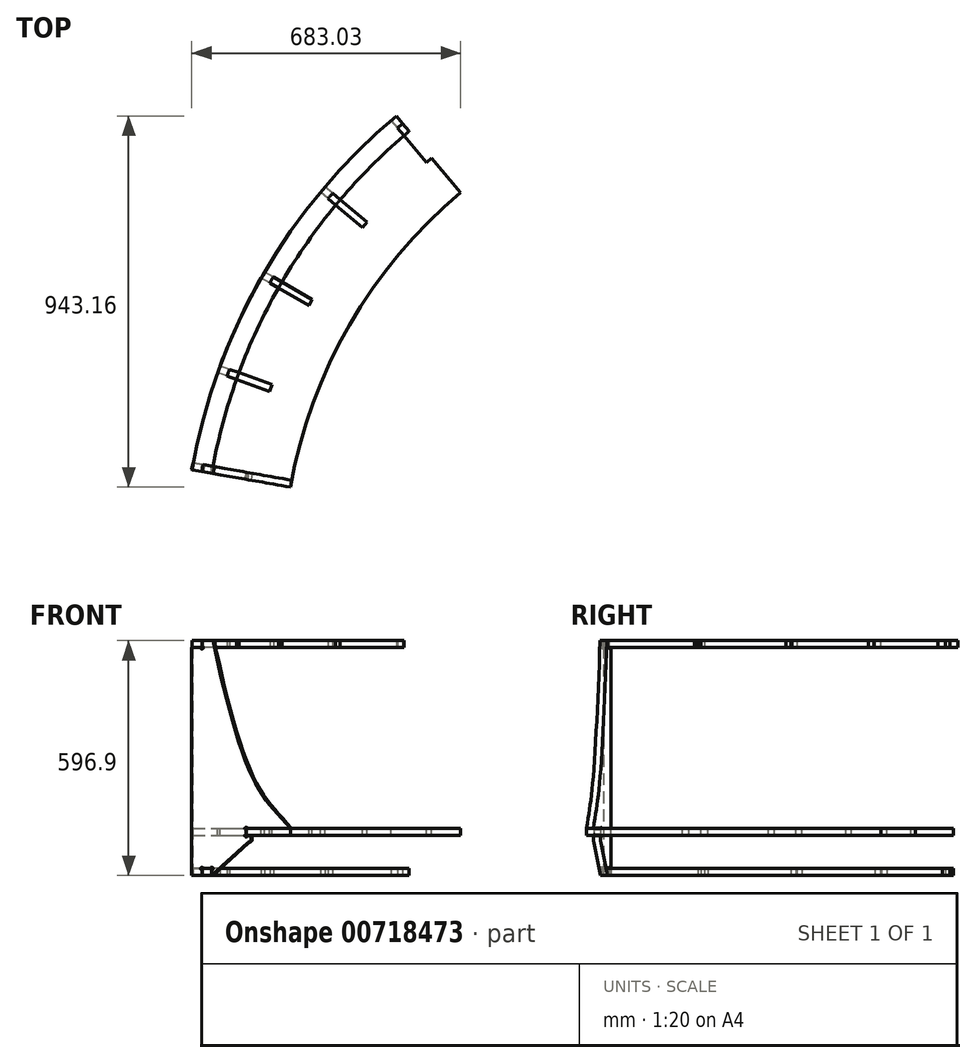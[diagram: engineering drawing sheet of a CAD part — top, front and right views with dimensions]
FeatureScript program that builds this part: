
annotation { "Feature Type Name" : "Feature", "Feature Type Description" : "" }
export const myFeature = defineFeature(function(context is Context, id is Id, definition is map)
    precondition{}
    {
        {
            var Q0;
            Q0=qCreatedBy(makeId("Top.planeOp"),FACE);
            var sketch = newSketch(context, id + "F0", { "sketchPlane" : qUnion([Q0])});
            skLineSegment(sketch, "E0", {"start": v(-959.2, 1143.13) * mm, "end": v(-942.87, 1123.67) * mm});
            skLineSegment(sketch, "E1", {"start": v(-1469.58, 259.13) * mm, "end": v(-1444.57, 254.72) * mm});
            skArc(sketch, "E2.trimOffspring", {"start": v(-989.08, 1151.08) * mm, "mid": v(-1076.28, 1070) * mm, "end": v(-1156.85, 982.32) * mm, "construction": true});
            skArc(sketch, "E3.trimOffspring", {"start": v(-942.87, 1123.67) * mm, "mid": v(-1270.33, 733.42) * mm, "end": v(-1444.57, 254.72) * mm});
            skArc(sketch, "E4.trimOffspring", {"start": v(-989.08, 1151.08) * mm, "mid": v(-1076.28, 1070) * mm, "end": v(-1156.85, 982.32) * mm});
            skLineSegment(sketch, "E5.0", {"start": v(-1287.86, 753.81) * mm, "end": v(-1309.88, 766.52) * mm});
            skLineSegment(sketch, "E6.0", {"start": v(-1296.75, 738.41) * mm, "end": v(-1318.77, 751.13) * mm});
            skLineSegment(sketch, "E7.0", {"start": v(-1399.2, 518.72) * mm, "end": v(-1423.08, 527.42) * mm});
            skLineSegment(sketch, "E8.0", {"start": v(-1405.27, 502.02) * mm, "end": v(-1429.17, 510.71) * mm});
            skLineSegment(sketch, "E9.0", {"start": v(-1137.4, 966) * mm, "end": v(-1156.87, 982.34) * mm});
            skLineSegment(sketch, "E10.0", {"start": v(-1148.82, 952.37) * mm, "end": v(-1168.3, 968.72) * mm});
            skLineSegment(sketch, "E11.0", {"start": v(-1491.5, 281.05) * mm, "end": v(-1466.39, 276.62) * mm});
            skLineSegment(sketch, "E12.0", {"start": v(-989.15, 1151.16) * mm, "end": v(-972.75, 1131.62) * mm});
            skArc(sketch, "E13.0", {"start": v(-959.2, 1143.13) * mm, "mid": v(-966, 1137.4) * mm, "end": v(-972.75, 1131.62) * mm});
            skArc(sketch, "E14.trimOffspring", {"start": v(-1466.39, 276.62) * mm, "mid": v(-1468, 267.88) * mm, "end": v(-1469.58, 259.13) * mm});
            skArc(sketch, "E15.trimOffspring", {"start": v(-1399.2, 518.72) * mm, "mid": v(-1402.26, 510.38) * mm, "end": v(-1405.27, 502.02) * mm});
            skArc(sketch, "E16.trimOffspring", {"start": v(-1287.86, 753.81) * mm, "mid": v(-1292.33, 746.12) * mm, "end": v(-1296.75, 738.41) * mm});
            skArc(sketch, "E17.trimOffspring", {"start": v(-1137.4, 966) * mm, "mid": v(-1143.13, 959.2) * mm, "end": v(-1148.82, 952.37) * mm});
            skArc(sketch, "E18.trimOffspring", {"start": v(-1168.28, 968.7) * mm, "mid": v(-1243.19, 870.49) * mm, "end": v(-1309.86, 766.51) * mm, "construction": true});
            skArc(sketch, "E19.trimOffspring", {"start": v(-1318.75, 751.11) * mm, "mid": v(-1375.46, 641.39) * mm, "end": v(-1423.06, 527.41) * mm, "construction": true});
            skArc(sketch, "E20.trimOffspring", {"start": v(-1318.75, 751.11) * mm, "mid": v(-1375.46, 641.39) * mm, "end": v(-1423.06, 527.41) * mm});
            skArc(sketch, "E21.trimOffspring", {"start": v(-1168.28, 968.7) * mm, "mid": v(-1243.19, 870.49) * mm, "end": v(-1309.86, 766.51) * mm});
            skArc(sketch, "E22.trimOffspring", {"start": v(-1429.14, 510.7) * mm, "mid": v(-1464.78, 397.09) * mm, "end": v(-1491.4, 281.03) * mm, "construction": true});
            skArc(sketch, "E23.trimOffspring", {"start": v(-1429.14, 510.7) * mm, "mid": v(-1464.78, 397.09) * mm, "end": v(-1491.4, 281.03) * mm});
            skSolve(sketch);
        }
        {
            var Q0;
            Q0=makeQuery(id+"F0.imprint","IMPRINT",FACE,{"disambiguationData":[TD([[makeQuery(id+"F0.imprint","IMPRINT",EDGE,{"derivedFrom":sQuery(id+"F0.wireOp",EDGE,"E0")}),-1.0]])]});
            extrude(context, id + "F1", {"entities" : qUnion([Q0]), "depth" : 17.78 * mm, "offsetDistance" : 25.4 * mm});
        }
        {
            var Q0;
            Q0=makeQuery(id+"F1.opExtrude","SWEPT_FACE",FACE,{"disambiguationData":[OSD([sQuery(id+"F0.wireOp",EDGE,"E1")])]});
            var sketch = newSketch(context, id + "F2", { "sketchPlane" : qUnion([Q0])});
            skLineSegment(sketch, "E24", {"start": v(-1492.25, 0) * mm, "end": v(-1518.36, 0) * mm});
            skLineSegment(sketch, "E25", {"start": v(-1518.36, 0) * mm, "end": v(-1518.36, 579.12) * mm});
            skPoint(sketch, "E26.endSnap0", {"position": v(-1365.25, 119.38) * mm});
            skLineSegment(sketch, "E27", {"start": v(-1492.25, 596.9) * mm, "end": v(-1492.25, 582.7) * mm});
            skLineSegment(sketch, "E28", {"start": v(-1481.14, 663.58) * mm, "end": v(-1476.38, 663.58) * mm});
            skLineSegment(sketch, "E29", {"start": v(-1365.25, 91.35) * mm, "end": v(-1365.25, 95.25) * mm});
            skArc(sketch, "E30.filletArc", {"start": v(-1365.25, 95.25) * mm, "mid": v(-1367.1, 99.74) * mm, "end": v(-1371.6, 101.6) * mm});
            skArc(sketch, "E31.filletArc", {"start": v(-1370.75, 85.06) * mm, "mid": v(-1366.82, 87.17) * mm, "end": v(-1365.25, 91.35) * mm});
            skPoint(sketch, "E32.visualSharp", {"position": v(-1263.65, 119.38) * mm});
            skPoint(sketch, "E33.start.orphan", {"position": v(-1263.65, 101.6) * mm});
            skLineSegment(sketch, "E34", {"start": v(-1374.15, 83.49) * mm, "end": v(-1466.85, 0) * mm});
            skLineSegment(sketch, "E35", {"start": v(-1518.36, 0) * mm, "end": v(-1492.25, 0) * mm});
            skLineSegment(sketch, "E36", {"start": v(-1492.25, 0) * mm, "end": v(-1492.25, 14.35) * mm});
            skLineSegment(sketch, "E37", {"start": v(-1488.82, 17.78) * mm, "end": v(-1470.3, 17.78) * mm});
            skLineSegment(sketch, "E38", {"start": v(-1466.85, 14.34) * mm, "end": v(-1466.85, 0) * mm});
            skArc(sketch, "E39.filletArc", {"start": v(-1370.75, 85.06) * mm, "mid": v(-1372.57, 84.53) * mm, "end": v(-1374.15, 83.49) * mm});
            skFitSpline(sketch, "E40", {"points": [v(-1476.38, 663.58) * mm, v(-1357.3, 240.57) * mm, v(-1263.65, 119.38) * mm], "startDerivative": vector(135.83, -714.5) * mm, "endDerivative": vector(297.84, -355.69) * mm});
            skLineSegment(sketch, "E41", {"start": v(-1495.58, 579.12) * mm, "end": v(-1518.36, 579.12) * mm});
            skLineSegment(sketch, "E42", {"start": v(-1492.25, 596.9) * mm, "end": v(-1463.1, 596.9) * mm});
            skLineSegment(sketch, "E43", {"start": v(-1374.52, 119.38) * mm, "end": v(-1263.65, 119.38) * mm});
            skLineSegment(sketch, "E44", {"start": v(-1377.95, 104.91) * mm, "end": v(-1377.95, 116.04) * mm});
            skLineSegment(sketch, "E45", {"start": v(-1374.58, 101.6) * mm, "end": v(-1371.6, 101.6) * mm});
            skArc(sketch, "E46", {"start": v(-1488.82, 17.78) * mm, "mid": v(-1494.67, 20.2) * mm, "end": v(-1492.25, 14.35) * mm});
            skArc(sketch, "E47", {"start": v(-1466.85, 14.34) * mm, "mid": v(-1464.44, 20.2) * mm, "end": v(-1470.3, 17.78) * mm});
            skArc(sketch, "E48", {"start": v(-1377.95, 104.91) * mm, "mid": v(-1380.4, 99.04) * mm, "end": v(-1374.58, 101.6) * mm});
            skArc(sketch, "E49", {"start": v(-1374.52, 119.38) * mm, "mid": v(-1380.34, 121.92) * mm, "end": v(-1377.95, 116.04) * mm});
            skArc(sketch, "E50", {"start": v(-1495.58, 579.12) * mm, "mid": v(-1489.64, 576.94) * mm, "end": v(-1492.25, 582.7) * mm});
            skSolve(sketch);
        }
        {
            var Q0;
            Q0=makeQuery(id+"F2.imprint","IMPRINT",FACE,{"disambiguationData":[TD([[makeQuery(id+"F2.imprint","IMPRINT",EDGE,{"derivedFrom":sQuery(id+"F2.wireOp",EDGE,"E25")}),-1.0]])]});
            extrude(context, id + "F3", {"entities" : qUnion([Q0]), "oppositeDirection" : true, "depth" : 17.78 * mm, "offsetDistance" : 25.4 * mm});
        }
        {
            var Q0;
            Q0=makeQuery(id+"F3.opExtrude","SWEPT_FACE",FACE,{"disambiguationData":[OSD([sQuery(id+"F2.wireOp",EDGE,"E41")])]});
            var sketch = newSketch(context, id + "F4", { "sketchPlane" : qUnion([Q0])});
            skArc(sketch, "E51.0", {"start": v(-1309.86, 766.51) * mm, "mid": v(-1375.46, 641.39) * mm, "end": v(-1429.14, 510.7) * mm});
            skArc(sketch, "E51.1", {"start": v(-956.42, 1112.16) * mm, "mid": v(-1040.36, 1034.07) * mm, "end": v(-1117.94, 949.67) * mm});
            skArc(sketch, "E51.2", {"start": v(-1168.28, 968.7) * mm, "mid": v(-1243.19, 870.49) * mm, "end": v(-1309.86, 766.51) * mm});
            skArc(sketch, "E51.3", {"start": v(-975.53, 1162.59) * mm, "mid": v(-1076.28, 1070) * mm, "end": v(-1168.28, 968.7) * mm});
            skArc(sketch, "E52.0", {"start": v(-1429.14, 510.7) * mm, "mid": v(-1467.08, 388.5) * mm, "end": v(-1494.6, 263.54) * mm});
            skLineSegment(sketch, "E53.0", {"start": v(-972.75, 1131.62) * mm, "end": v(-956.42, 1112.16) * mm});
            skLineSegment(sketch, "E53.2", {"start": v(-975.53, 1162.59) * mm, "end": v(-959.2, 1143.13) * mm});
            skArc(sketch, "E54.0", {"start": v(-1399.2, 518.72) * mm, "mid": v(-1402.26, 510.38) * mm, "end": v(-1405.27, 502.02) * mm});
            skArc(sketch, "E54.1", {"start": v(-1287.86, 753.81) * mm, "mid": v(-1292.33, 746.12) * mm, "end": v(-1296.75, 738.41) * mm});
            skArc(sketch, "E54.2", {"start": v(-1137.4, 966) * mm, "mid": v(-1143.13, 959.2) * mm, "end": v(-1148.82, 952.37) * mm});
            skLineSegment(sketch, "E55", {"start": v(-1494.6, 263.54) * mm, "end": v(-1469.58, 259.13) * mm});
            skLineSegment(sketch, "E56", {"start": v(-1469.58, 259.13) * mm, "end": v(-1466.5, 276.64) * mm});
            skLineSegment(sketch, "E57", {"start": v(-1441.37, 272.2) * mm, "end": v(-1466.5, 276.64) * mm});
            skPoint(sketch, "E51.4.end.orphan", {"position": v(-1244.45, 219.43) * mm});
            skPoint(sketch, "E51.5.end.orphan", {"position": v(-1241.36, 236.94) * mm});
            skLineSegment(sketch, "E58", {"start": v(-1399.2, 518.72) * mm, "end": v(-1375.32, 510.04) * mm});
            skLineSegment(sketch, "E59", {"start": v(-1405.27, 502.02) * mm, "end": v(-1381.4, 493.33) * mm});
            skLineSegment(sketch, "E60", {"start": v(-1296.75, 738.41) * mm, "end": v(-1274.75, 725.71) * mm});
            skLineSegment(sketch, "E61", {"start": v(-1287.86, 753.81) * mm, "end": v(-1265.86, 741.11) * mm});
            skLineSegment(sketch, "E62", {"start": v(-1148.82, 952.37) * mm, "end": v(-1129.37, 936.05) * mm});
            skLineSegment(sketch, "E63", {"start": v(-1137.4, 966) * mm, "end": v(-1117.94, 949.67) * mm});
            skArc(sketch, "E64.trimOffspring", {"start": v(-1381.4, 493.33) * mm, "mid": v(-1415.71, 383.94) * mm, "end": v(-1441.37, 272.2) * mm});
            skPoint(sketch, "E65.orphan", {"position": v(-1423.06, 527.41) * mm});
            skPoint(sketch, "E66.orphan", {"position": v(-1156.85, 982.32) * mm});
            skArc(sketch, "E67.trimOffspring", {"start": v(-1129.37, 936.05) * mm, "mid": v(-1201.57, 841.35) * mm, "end": v(-1265.86, 741.11) * mm});
            skPoint(sketch, "E68.orphan", {"position": v(-1318.75, 751.11) * mm});
            skArc(sketch, "E69.trimOffspring", {"start": v(-1274.75, 725.71) * mm, "mid": v(-1329.42, 619.92) * mm, "end": v(-1375.32, 510.04) * mm});
            skLineSegment(sketch, "E70", {"start": v(-1469.58, 259.13) * mm, "end": v(-1494.6, 263.54) * mm});
            skPoint(sketch, "E53.1.start.orphan", {"position": v(-959.2, 1143.13) * mm});
            skPoint(sketch, "E71.orphan", {"position": v(-972.75, 1131.62) * mm});
            skPoint(sketch, "E72.orphan", {"position": v(-989.08, 1151.08) * mm});
            skLineSegment(sketch, "E73", {"start": v(-972.75, 1131.62) * mm, "end": v(-959.2, 1143.13) * mm});
            skPoint(sketch, "E74.orphan", {"position": v(-942.87, 1123.67) * mm});
            skSolve(sketch);
        }
        {
            var Q0;
            Q0 = qSketchRegion(id + "F4", true);
            extrude(context, id + "F5", {"entities" : qUnion([Q0]), "depth" : 17.78 * mm, "offsetDistance" : 25.4 * mm});
        }
        {
            var Q0;
            Q0=makeQuery(id+"F3.opExtrude","SWEPT_FACE",FACE,{"disambiguationData":[OSD([sQuery(id+"F2.wireOp",EDGE,"E43")])]});
            var sketch = newSketch(context, id + "F6", { "sketchPlane" : qUnion([Q0])});
            skSolve(sketch);
        }
        {
            var Q0;
            {var subQ0=sQuery(id+"F2.wireOp",EDGE,"E43");Q0=makeQuery(id+"F6.imprint","IMPRINT",FACE,{"disambiguationData":[TD([[makeQuery(id+"F6.imprint","IMPRINT",EDGE,{"derivedFrom":makeQuery(id+"F3.opExtrude","CAP_EDGE",EDGE,{"disambiguationData":[OSD([subQ0])],"isStart":true})}),-1.0]])]});}
            var sketch = newSketch(context, id + "F7", { "sketchPlane" : qUnion([Q0])});
            skLineSegment(sketch, "E75.0", {"start": v(-1353.93, -256.79) * mm, "end": v(-1357.02, -239.28) * mm});
            skArc(sketch, "E76", {"start": v(-1357.02, -239.28) * mm, "mid": v(-1193.34, -688.98) * mm, "end": v(-885.73, -1055.57) * mm, "construction": true});
            skArc(sketch, "E77", {"start": v(-1244.45, -219.43) * mm, "mid": v(-1094.35, -631.83) * mm, "end": v(-812.26, -968.01) * mm});
            skArc(sketch, "E78.0", {"start": v(-1429.14, -510.7) * mm, "mid": v(-1464.78, -397.09) * mm, "end": v(-1491.4, -281.03) * mm});
            skArc(sketch, "E79.0", {"start": v(-1318.75, -751.11) * mm, "mid": v(-1375.46, -641.39) * mm, "end": v(-1423.06, -527.41) * mm});
            skArc(sketch, "E80.0", {"start": v(-1168.28, -968.7) * mm, "mid": v(-1243.19, -870.49) * mm, "end": v(-1309.86, -766.51) * mm});
            skArc(sketch, "E81.0", {"start": v(-989.08, -1151.08) * mm, "mid": v(-1076.28, -1070) * mm, "end": v(-1156.85, -982.32) * mm});
            skLineSegment(sketch, "E82.0", {"start": v(-1197.76, -681.26) * mm, "end": v(-1318.75, -751.11) * mm});
            skLineSegment(sketch, "E83.0", {"start": v(-1188.87, -696.66) * mm, "end": v(-1309.86, -766.51) * mm});
            skLineSegment(sketch, "E84.0", {"start": v(-1049.83, -892.52) * mm, "end": v(-1156.85, -982.32) * mm});
            skLineSegment(sketch, "E85.0", {"start": v(-1061.26, -878.9) * mm, "end": v(-1168.28, -968.7) * mm});
            skPoint(sketch, "E86.orphan", {"position": v(-1429.14, -510.7) * mm});
            skPoint(sketch, "E87.orphan", {"position": v(-1423.06, -527.41) * mm});
            skPoint(sketch, "E88.orphan", {"position": v(-1318.75, -751.11) * mm});
            skPoint(sketch, "E89.orphan", {"position": v(-1168.28, -968.7) * mm});
            skPoint(sketch, "E90.orphan", {"position": v(-1156.85, -982.32) * mm});
            skLineSegment(sketch, "E91.0", {"start": v(-989.08, -1151.08) * mm, "end": v(-899.28, -1044.05) * mm});
            skPoint(sketch, "E92.orphan", {"position": v(-1309.86, -766.51) * mm});
            skPoint(sketch, "E93.orphan", {"position": v(-1444.57, -254.72) * mm});
            skLineSegment(sketch, "E94.trimOffspring", {"start": v(-885.73, -1055.57) * mm, "end": v(-812.26, -968.01) * mm});
            skLineSegment(sketch, "E95", {"start": v(-1061.26, -878.9) * mm, "end": v(-1049.83, -892.52) * mm});
            skLineSegment(sketch, "E96", {"start": v(-899.28, -1044.05) * mm, "end": v(-885.73, -1055.57) * mm});
            skLineSegment(sketch, "E97", {"start": v(-1197.76, -681.26) * mm, "end": v(-1188.87, -696.66) * mm});
            skLineSegment(sketch, "E98", {"start": v(-1297.86, -462.92) * mm, "end": v(-1291.78, -479.63) * mm});
            skLineSegment(sketch, "E99", {"start": v(-1491.4, -281.03) * mm, "end": v(-1353.93, -256.79) * mm});
            skLineSegment(sketch, "E100", {"start": v(-1357.02, -239.28) * mm, "end": v(-1244.45, -219.43) * mm});
            skLineSegment(sketch, "E101", {"start": v(-1429.14, -510.7) * mm, "end": v(-1297.86, -462.92) * mm});
            skLineSegment(sketch, "E102", {"start": v(-1423.06, -527.41) * mm, "end": v(-1291.78, -479.63) * mm});
            skSolve(sketch);
        }
        {
            var Q0;
            Q0 = qSketchRegion(id + "F7", true);
            extrude(context, id + "F8", {"entities" : qUnion([Q0]), "depth" : 17.78 * mm, "offsetDistance" : 25.4 * mm});
        }
    });
